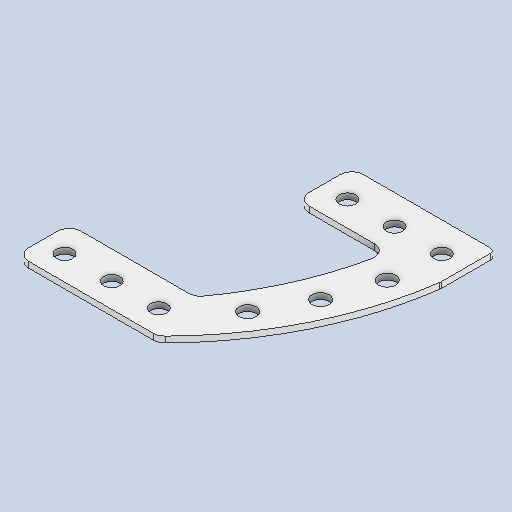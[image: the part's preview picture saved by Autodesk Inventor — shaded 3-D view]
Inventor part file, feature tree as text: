
AUTODESK INVENTOR PART (.ipt)
format: ipt  version: 2025.2 (Build 292293000, 293)  size: 137,216 bytes
history: native  units: in
note: dims shown in document units (in); Inventor stores cm internally (conversion verified against a paired STEP export)
features: extrude x1, sketch x1
ambient origin geometry x8: Origin, YZ Plane, XZ Plane, XY Plane, X Axis, Y Axis, Z Axis, Center Point
bodies: Solid1 (feature_tree)
feature tree (2):
  extrude  "Extrusion1"  Depth=0.0625in TaperAngle=0.0deg
  sketch  "Sketch1"  dims[d0=0.125in d1=0.125in d2=0.05in d3=0.182in d4=0.182in d5=0.182in d6=0.0625in d7=0.0in]
